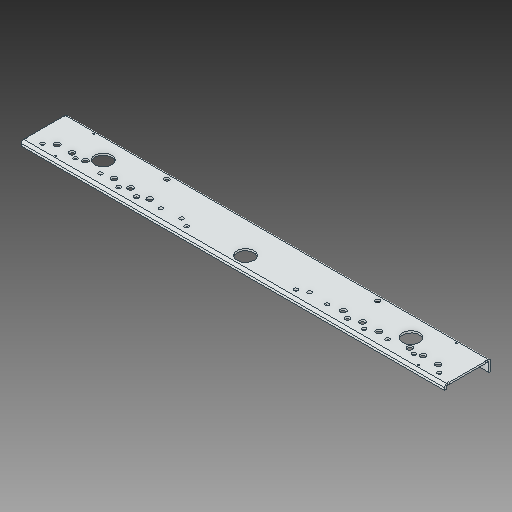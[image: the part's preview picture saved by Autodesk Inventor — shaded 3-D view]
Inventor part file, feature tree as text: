
AUTODESK INVENTOR PART (.ipt)
format: ipt  version: 2017 (Build 210142000, 142)  size: 223,232 bytes
history: native  units: in
note: dims shown in document units (in); Inventor stores cm internally (conversion verified against a paired STEP export)
features: other x4, reference x2, extrude x1, sketch x1
ambient origin geometry x8: Origin, YZ Plane, XZ Plane, XY Plane, X Axis, Y Axis, Z Axis, Center Point
bodies: Solid1 (feature_tree)
feature tree (8):
  extrude  "Extrusion1"  [1 undecoded]
  sketch  "Sketch1"  dims[d0=0.0in d1=0.0in]
  reference  "Reference1"
  reference  "Reference2"
  other  "Cut-Extrude10"
  other  "<userpath>\Documents\Inventor\2017 Robot\Robot Chassis.iam"
  other  "Robot Chassis.iam"
  other  "am-2952a_AM14U3_Inside_Plate:1"
note: 1 required parameter value undecoded (feature->parameter linkage not recoverable at this tier; creation-order binding heuristic only, values carry confidence <= 0.55)
